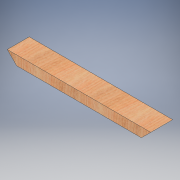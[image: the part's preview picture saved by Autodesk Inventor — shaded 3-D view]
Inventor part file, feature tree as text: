
AUTODESK INVENTOR PART (.ipt)
format: ipt  version: 2016 (Build 200138000, 138)  size: 105,472 bytes
history: native  units: in
note: dims shown in document units (in); Inventor stores cm internally (conversion verified against a paired STEP export)
features: extrude x1, sketch x1
ambient origin geometry x8: Origin, YZ Plane, XZ Plane, XY Plane, X Axis, Y Axis, Z Axis, Center Point
bodies: Body1 (feature_tree)
feature tree (2):
  extrude  "Extrusion2"  TaperAngle=135.0deg  [1 undecoded]
  sketch  "Sketch2"  dims[d10=45.0deg d11=135.0deg d12=3.5in d13=0.0in d14=22.9in d15=1.5in]
note: 1 required parameter value undecoded (feature->parameter linkage not recoverable at this tier; creation-order binding heuristic only, values carry confidence <= 0.55)
